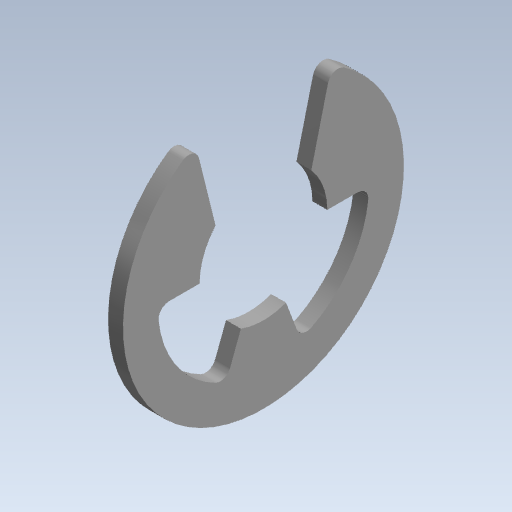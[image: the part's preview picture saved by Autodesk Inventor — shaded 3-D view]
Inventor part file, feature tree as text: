
AUTODESK INVENTOR PART (.ipt)
format: ipt  version: 2020 (Build 240168000, 168)  size: 86,528 bytes
history: native  units: mm (DEFAULTED — no unit token found)
features: fillet x1
ambient origin geometry x8: Origin, YZ Plane, XZ Plane, XY Plane, X Axis, Y Axis, Z Axis, Center Point
bodies: Solid1 (feature_tree)
feature tree (1):
  fillet  "Fillet1"  [1 undecoded]
note: 1 required parameter value undecoded (feature->parameter linkage not recoverable at this tier; creation-order binding heuristic only, values carry confidence <= 0.55)
